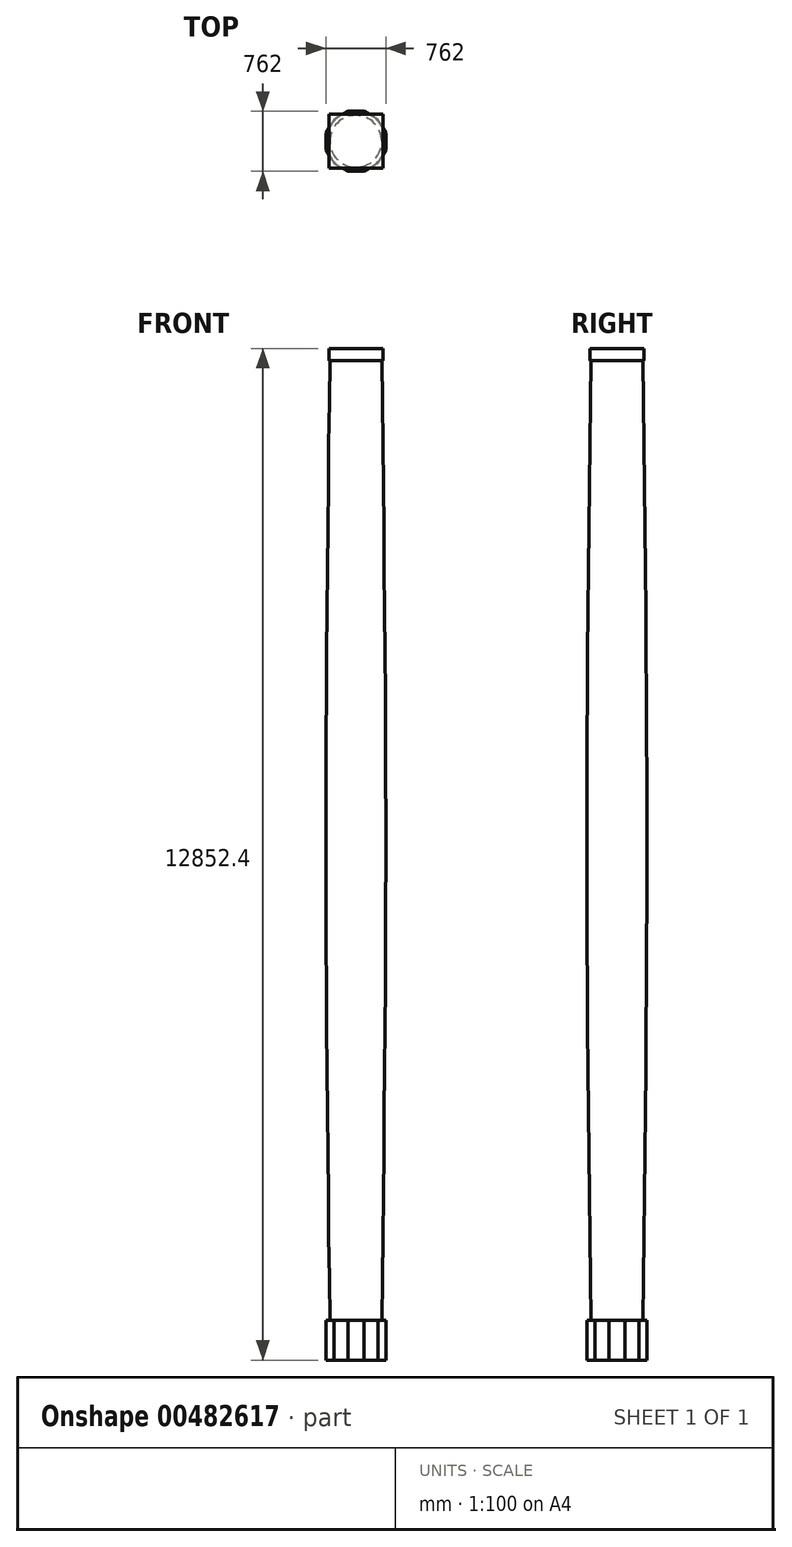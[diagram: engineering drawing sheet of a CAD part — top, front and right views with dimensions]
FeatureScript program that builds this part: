
annotation { "Feature Type Name" : "Feature", "Feature Type Description" : "" }
export const myFeature = defineFeature(function(context is Context, id is Id, definition is map)
    precondition{}
    {
        {
            var Q0;
            Q0=qCreatedBy(makeId("Top.planeOp"),FACE);
            var sketch = newSketch(context, id + "F0", { "sketchPlane" : qUnion([Q0])});
            skCircle(sketch, "E0", {"center": v(0, 0) * mm, "radius": 330.2 * mm});
            skSolve(sketch);
        }
        {
            var Q0;
            Q0=qCreatedBy(makeId("Top.planeOp"),FACE);
            cPlane(context, id + "F1", {"entities" : qUnion([Q0]), "cplaneType" : CPlaneType.OFFSET, "offset" : 6096 * mm, "width" : 152.4 * mm, "height" : 152.4 * mm});
        }
        {
            var Q0;
            Q0=qCreatedBy(id+"F1.planeOp",FACE);
            var sketch = newSketch(context, id + "F2", { "sketchPlane" : qUnion([Q0])});
            skCircle(sketch, "E1", {"center": v(0, 0) * mm, "radius": 381 * mm});
            skSolve(sketch);
        }
        {
            var Q0;
            Q0=qCreatedBy(id+"F1.planeOp",FACE);
            cPlane(context, id + "F3", {"entities" : qUnion([Q0]), "cplaneType" : CPlaneType.OFFSET, "offset" : 6096 * mm, "width" : 152.4 * mm, "height" : 152.4 * mm});
        }
        {
            var Q0;
            Q0=qCreatedBy(id+"F3.planeOp",FACE);
            var sketch = newSketch(context, id + "F4", { "sketchPlane" : qUnion([Q0])});
            skCircle(sketch, "E2", {"center": v(0, 0) * mm, "radius": 330.2 * mm});
            skSolve(sketch);
        }
        {
            var Q0;
            Q0=makeQuery(id+"F0.imprint","IMPRINT",FACE,{"disambiguationData":[TD([[makeQuery(id+"F0.imprint","IMPRINT",EDGE,{"derivedFrom":sQuery(id+"F0.wireOp",EDGE,"E0")}),1.0]])]});
            var Q1;
            Q1=makeQuery(id+"F2.imprint","IMPRINT",FACE,{"disambiguationData":[TD([[makeQuery(id+"F2.imprint","IMPRINT",EDGE,{"derivedFrom":sQuery(id+"F2.wireOp",EDGE,"E1")}),1.0]])]});
            var Q2;
            Q2=makeQuery(id+"F4.imprint","IMPRINT",FACE,{"disambiguationData":[TD([[makeQuery(id+"F4.imprint","IMPRINT",EDGE,{"derivedFrom":sQuery(id+"F4.wireOp",EDGE,"E2")}),1.0]])]});
            loft(context, id + "F5", {"sheetProfilesArray" : [{ "sheetProfileEntities" : qUnion([Q0]) }, { "sheetProfileEntities" : qUnion([Q1]) }, { "sheetProfileEntities" : qUnion([Q2]) }]});
        }
        {
            var Q0;
            Q0=makeQuery(id+"F5.opLoft","CAP_FACE",FACE,{"disambiguationData":[OSD([makeQuery(id+"F4.imprint","IMPRINT",FACE,{"disambiguationData":[TD([[makeQuery(id+"F4.imprint","IMPRINT",EDGE,{"derivedFrom":sQuery(id+"F4.wireOp",EDGE,"E2")}),1.0]])]})])],"isStart":true});
            var sketch = newSketch(context, id + "F6", { "sketchPlane" : qUnion([Q0])});
            skLineSegment(sketch, "E3.bottom", {"start": v(342.9, 342.9) * mm, "end": v(-342.9, 342.9) * mm});
            skLineSegment(sketch, "E3.top", {"start": v(342.9, -342.9) * mm, "end": v(-342.9, -342.9) * mm});
            skLineSegment(sketch, "E3.left", {"start": v(342.9, 342.9) * mm, "end": v(342.9, -342.9) * mm});
            skLineSegment(sketch, "E3.right", {"start": v(-342.9, 342.9) * mm, "end": v(-342.9, -342.9) * mm});
            skPoint(sketch, "E3.middle", {"position": v(0, 0) * mm});
            skSolve(sketch);
        }
        {
            var Q0;
            Q0 = qSketchRegion(id + "F6", true);
            extrude(context, id + "F7", {"entities" : qUnion([Q0]), "operationType" : NewBodyOperationType.ADD, "depth" : 152.4 * mm});
        }
        {
            var Q0;
            Q0=makeQuery(id+"F5.opLoft","CAP_FACE",FACE,{"disambiguationData":[OSD([makeQuery(id+"F0.imprint","IMPRINT",FACE,{"disambiguationData":[TD([[makeQuery(id+"F0.imprint","IMPRINT",EDGE,{"derivedFrom":sQuery(id+"F0.wireOp",EDGE,"E0")}),1.0]])]})])],"isStart":true});
            var sketch = newSketch(context, id + "F8", { "sketchPlane" : qUnion([Q0])});
            skCircle(sketch, "E4.cCircle", {"center": v(0, 0) * mm, "radius": 381 * mm, "construction": true});
            skLineSegment(sketch, "E4.0", {"start": v(102.09, -381) * mm, "end": v(-102.09, -381) * mm});
            skLineSegment(sketch, "E4.1", {"start": v(-102.09, -381) * mm, "end": v(-278.91, -278.91) * mm});
            skLineSegment(sketch, "E4.2", {"start": v(-278.91, -278.91) * mm, "end": v(-381, -102.09) * mm});
            skLineSegment(sketch, "E4.3", {"start": v(-381, -102.09) * mm, "end": v(-381, 102.09) * mm});
            skLineSegment(sketch, "E4.4", {"start": v(-381, 102.09) * mm, "end": v(-278.91, 278.91) * mm});
            skLineSegment(sketch, "E4.5", {"start": v(-278.91, 278.91) * mm, "end": v(-102.09, 381) * mm});
            skLineSegment(sketch, "E4.6", {"start": v(-102.09, 381) * mm, "end": v(102.09, 381) * mm});
            skLineSegment(sketch, "E4.7", {"start": v(102.09, 381) * mm, "end": v(278.91, 278.91) * mm});
            skLineSegment(sketch, "E4.8", {"start": v(278.91, 278.91) * mm, "end": v(381, 102.09) * mm});
            skLineSegment(sketch, "E4.9", {"start": v(381, 102.09) * mm, "end": v(381, -102.09) * mm});
            skLineSegment(sketch, "E4.10", {"start": v(381, -102.09) * mm, "end": v(278.91, -278.91) * mm});
            skLineSegment(sketch, "E4.11", {"start": v(278.91, -278.91) * mm, "end": v(102.09, -381) * mm});
            skPoint(sketch, "E4.0.midPoint", {"position": v(0, -381) * mm});
            skSolve(sketch);
        }
        {
            var Q0;
            Q0 = qSketchRegion(id + "F8", true);
            extrude(context, id + "F9", {"entities" : qUnion([Q0]), "operationType" : NewBodyOperationType.ADD, "depth" : 508 * mm});
        }
    });
